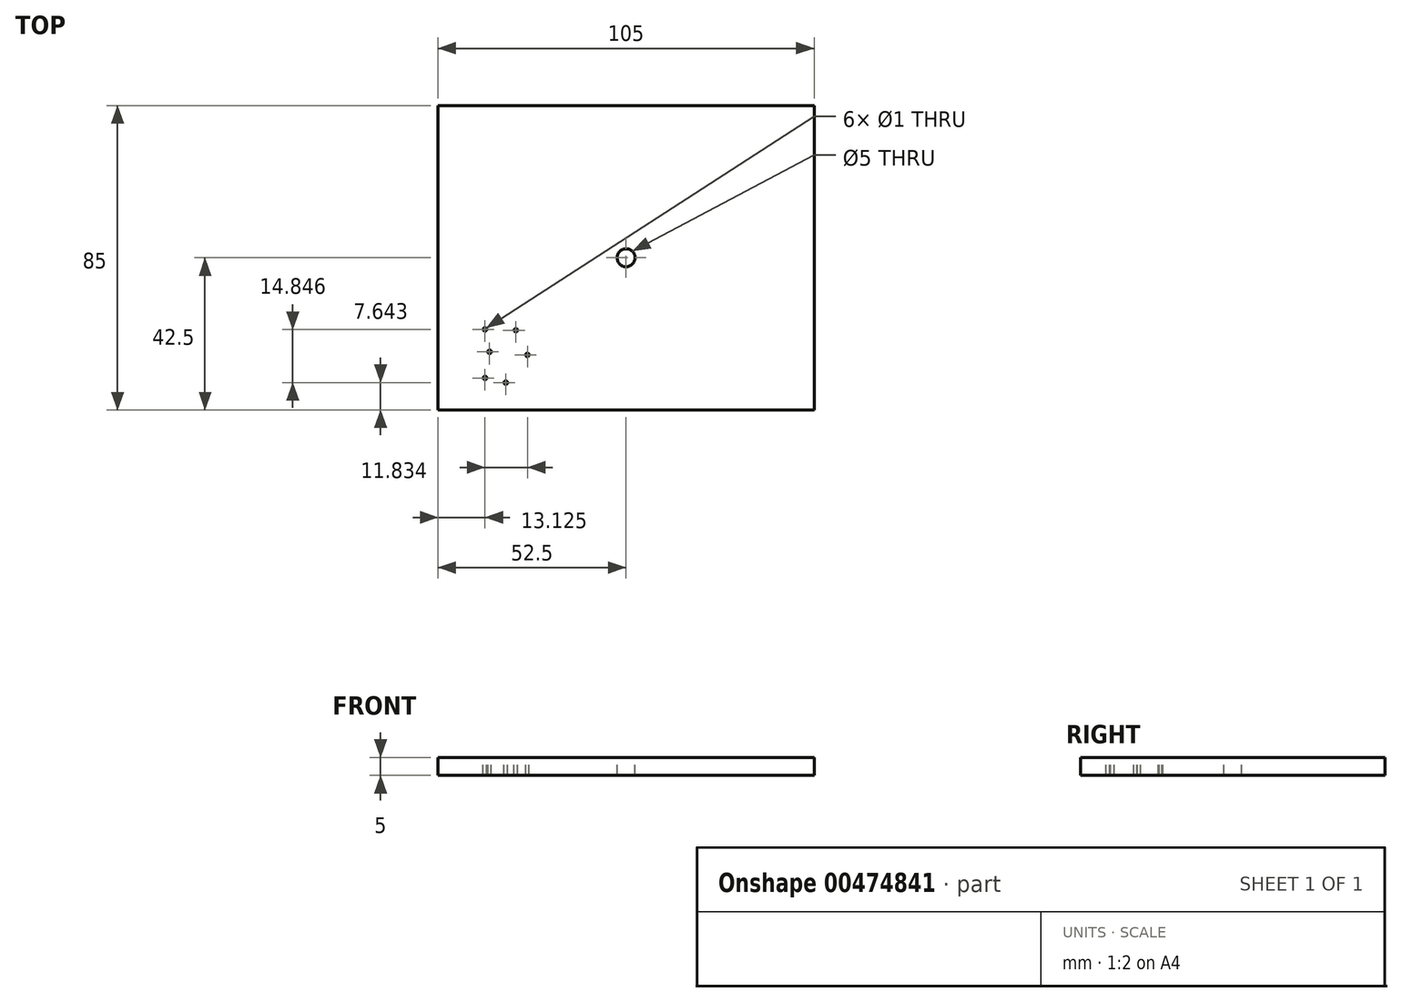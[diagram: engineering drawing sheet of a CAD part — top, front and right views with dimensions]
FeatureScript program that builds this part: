
annotation { "Feature Type Name" : "Feature", "Feature Type Description" : "" }
export const myFeature = defineFeature(function(context is Context, id is Id, definition is map)
    precondition{}
    {
        {
            var Q0;
            Q0=qCreatedBy(makeId("Top.planeOp"),FACE);
            var sketch = newSketch(context, id + "F0", { "sketchPlane" : qUnion([Q0])});
            skLineSegment(sketch, "E0.bottom", {"start": v(-52.5, 42.5) * mm, "end": v(52.5, 42.5) * mm});
            skLineSegment(sketch, "E0.top", {"start": v(-52.5, -42.5) * mm, "end": v(52.5, -42.5) * mm});
            skLineSegment(sketch, "E0.left", {"start": v(-52.5, 42.5) * mm, "end": v(-52.5, -42.5) * mm});
            skLineSegment(sketch, "E0.right", {"start": v(52.5, 42.5) * mm, "end": v(52.5, -42.5) * mm});
            skPoint(sketch, "E0.middle", {"position": v(0, 0) * mm});
            skSolve(sketch);
        }
        {
            var Q0;
            Q0 = qSketchRegion(id + "F0", true);
            extrude(context, id + "F1", {"entities" : qUnion([Q0]), "depth" : 2.5 * mm});
        }
        {
            var Q0;
            Q0=makeQuery(id+"F1.opExtrude","CAP_FACE",FACE,{"disambiguationData":[OSD([sQuery(id+"F0.wireOp",EDGE,"E0.bottom"),sQuery(id+"F0.wireOp",EDGE,"E0.top"),sQuery(id+"F0.wireOp",EDGE,"E0.left"),sQuery(id+"F0.wireOp",EDGE,"E0.right")])],"isStart":false});
            extrude(context, id + "F2", {"entities" : qUnion([Q0]), "operationType" : NewBodyOperationType.ADD, "depth" : 2.5 * mm});
        }
        {
            var Q0;
            Q0=makeQuery(id+"F2.opExtrude","CAP_FACE",FACE,{"disambiguationData":[OSD([sQuery(id+"F0.wireOp",EDGE,"E0.bottom"),sQuery(id+"F0.wireOp",EDGE,"E0.top"),sQuery(id+"F0.wireOp",EDGE,"E0.left"),sQuery(id+"F0.wireOp",EDGE,"E0.right")])],"isStart":false});
            var sketch = newSketch(context, id + "F3", { "sketchPlane" : qUnion([Q0])});
            skCircle(sketch, "E1", {"center": v(0, 0) * mm, "radius": 2.5 * mm});
            skCircle(sketch, "E2", {"center": v(-38.08, -26.25) * mm, "radius": 0.5 * mm});
            skCircle(sketch, "E3", {"center": v(-27.54, -27.11) * mm, "radius": 0.5 * mm});
            skCircle(sketch, "E4", {"center": v(-30.77, -20.23) * mm, "radius": 0.5 * mm});
            skCircle(sketch, "E5", {"center": v(-39.37, -20.01) * mm, "radius": 0.5 * mm});
            skCircle(sketch, "E6", {"center": v(-33.57, -34.86) * mm, "radius": 0.5 * mm});
            skCircle(sketch, "E7", {"center": v(-39.37, -33.57) * mm, "radius": 0.5 * mm});
            skSolve(sketch);
        }
        {
            var Q0;
            Q0 = qSketchRegion(id + "F3", true);
            extrude(context, id + "F4", {"entities" : qUnion([Q0]), "operationType" : NewBodyOperationType.REMOVE, "oppositeDirection" : true, "depth" : 25 * mm});
        }
    });
